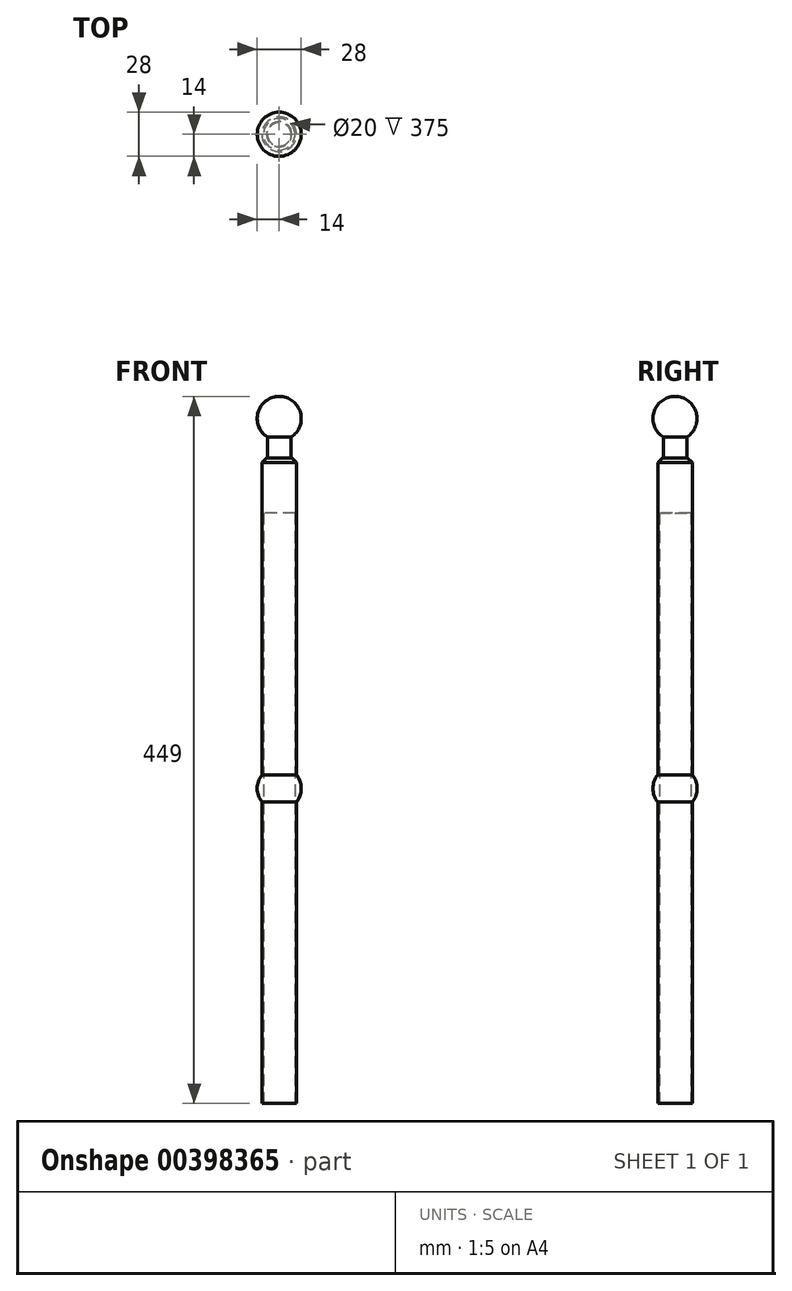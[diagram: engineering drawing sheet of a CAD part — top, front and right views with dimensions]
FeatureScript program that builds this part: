
annotation { "Feature Type Name" : "Feature", "Feature Type Description" : "" }
export const myFeature = defineFeature(function(context is Context, id is Id, definition is map)
    precondition{}
    {
        {
            var Q0;
            Q0=qCreatedBy(makeId("Top.planeOp"),FACE);
            var sketch = newSketch(context, id + "F0", { "sketchPlane" : qUnion([Q0])});
            skCircle(sketch, "E0", {"center": v(0, 0) * mm, "radius": 11 * mm});
            skCircle(sketch, "E1", {"center": v(0, 0) * mm, "radius": 10 * mm});
            skSolve(sketch);
        }
        {
            var Q0;
            Q0 = qSketchRegion(id + "F0", true);
            extrude(context, id + "F1", {"entities" : qUnion([Q0]), "endBound" : BoundingType.SYMMETRIC, "depth" : 400 * mm});
        }
        {
            var Q0;
            Q0=qCreatedBy(makeId("Front.planeOp"),FACE);
            var sketch = newSketch(context, id + "F2", { "sketchPlane" : qUnion([Q0])});
            skArc(sketch, "E2", {"start": v(10, -9.8) * mm, "mid": v(14, 0) * mm, "end": v(10, 9.8) * mm});
            skLineSegment(sketch, "E3", {"start": v(10, 9.8) * mm, "end": v(10, -9.8) * mm});
            skSolve(sketch);
        }
        {
            var Q0;
            Q0 = qSketchRegion(id + "F2", true);
            var Q1;
            Q1=makeQuery(id+"F1.opExtrude","SWEPT_FACE",FACE,{"disambiguationData":[OSD([sQuery(id+"F0.wireOp",EDGE,"E0")])]});
            revolve(context, id + "F3", {"operationType" : NewBodyOperationType.ADD, "entities" : qUnion([Q0]), "axis" : qUnion([Q1]), "revolveType" : RevolveType.FULL});
        }
        {
            var Q0;
            Q0=makeQuery(id+"F1.opExtrude","CAP_FACE",FACE,{"disambiguationData":[OSD([sQuery(id+"F0.wireOp",EDGE,"E0"),sQuery(id+"F0.wireOp",EDGE,"E1")])],"isStart":false});
            var sketch = newSketch(context, id + "F4", { "sketchPlane" : qUnion([Q0])});
            skCircle(sketch, "E4", {"center": v(0, 0) * mm, "radius": 10 * mm});
            skCircle(sketch, "E5", {"center": v(0, 0) * mm, "radius": 11 * mm});
            skCircle(sketch, "E6", {"center": v(0, 0) * mm, "radius": 7.5 * mm});
            skSolve(sketch);
        }
        {
            var Q0;
            Q0=makeQuery(id+"F4.imprint","IMPRINT",FACE,{"disambiguationData":[TD([[makeQuery(id+"F4.imprint","IMPRINT",EDGE,{"derivedFrom":sQuery(id+"F4.wireOp",EDGE,"E4")}),1.0]])]});
            var Q1;
            Q1=makeQuery(id+"F4.imprint","IMPRINT",FACE,{"disambiguationData":[TD([[makeQuery(id+"F4.imprint","IMPRINT",EDGE,{"derivedFrom":sQuery(id+"F4.wireOp",EDGE,"E6")}),1.0]])]});
            extrude(context, id + "F5", {"entities" : qUnion([Q0, Q1]), "oppositeDirection" : true, "depth" : 25 * mm});
        }
        {
            var Q0;
            Q0=makeQuery(id+"F4.imprint","IMPRINT",FACE,{"disambiguationData":[TD([[makeQuery(id+"F4.imprint","IMPRINT",EDGE,{"derivedFrom":sQuery(id+"F4.wireOp",EDGE,"E4")}),-1.0]])]});
            var Q1;
            Q1=makeQuery(id+"F4.imprint","IMPRINT",FACE,{"disambiguationData":[TD([[makeQuery(id+"F4.imprint","IMPRINT",EDGE,{"derivedFrom":sQuery(id+"F4.wireOp",EDGE,"E4")}),1.0]])]});
            extrude(context, id + "F6", {"entities" : qUnion([Q0, Q1]), "operationType" : NewBodyOperationType.ADD, "depth" : 10 * mm});
        }
        {
            var Q0;
            Q0=makeQuery(id+"F4.imprint","IMPRINT",FACE,{"disambiguationData":[TD([[makeQuery(id+"F4.imprint","IMPRINT",EDGE,{"derivedFrom":sQuery(id+"F4.wireOp",EDGE,"E6")}),1.0]])]});
            extrude(context, id + "F7", {"entities" : qUnion([Q0]), "operationType" : NewBodyOperationType.ADD, "depth" : 35 * mm});
        }
        {
            var Q0;
            Q0=makeQuery(id+"F6.opExtrude","CAP_EDGE",EDGE,{"disambiguationData":[OSD([sQuery(id+"F4.wireOp",EDGE,"E5")])],"isStart":false});
            chamfer(context, id + "F8", {"entities" : qUnion([Q0]), "width" : 3 * mm, "tangentPropagation" : true});
        }
        {
            var Q0;
            Q0=qCreatedBy(makeId("Front.planeOp"),FACE);
            var sketch = newSketch(context, id + "F9", { "sketchPlane" : qUnion([Q0])});
            skArc(sketch, "E7", {"start": v(0, 221) * mm, "mid": v(14, 235) * mm, "end": v(0, 249) * mm});
            skLineSegment(sketch, "E8", {"start": v(0, 249) * mm, "end": v(0, 221) * mm});
            skSolve(sketch);
        }
        {
            var Q0;
            Q0 = qSketchRegion(id + "F9", true);
            var Q1;
            Q1=makeQuery(id+"F7.opExtrude","SWEPT_FACE",FACE,{"disambiguationData":[OSD([sQuery(id+"F4.wireOp",EDGE,"E6")])]});
            revolve(context, id + "F10", {"operationType" : NewBodyOperationType.ADD, "entities" : qUnion([Q0]), "axis" : qUnion([Q1]), "revolveType" : RevolveType.FULL});
        }
    });
